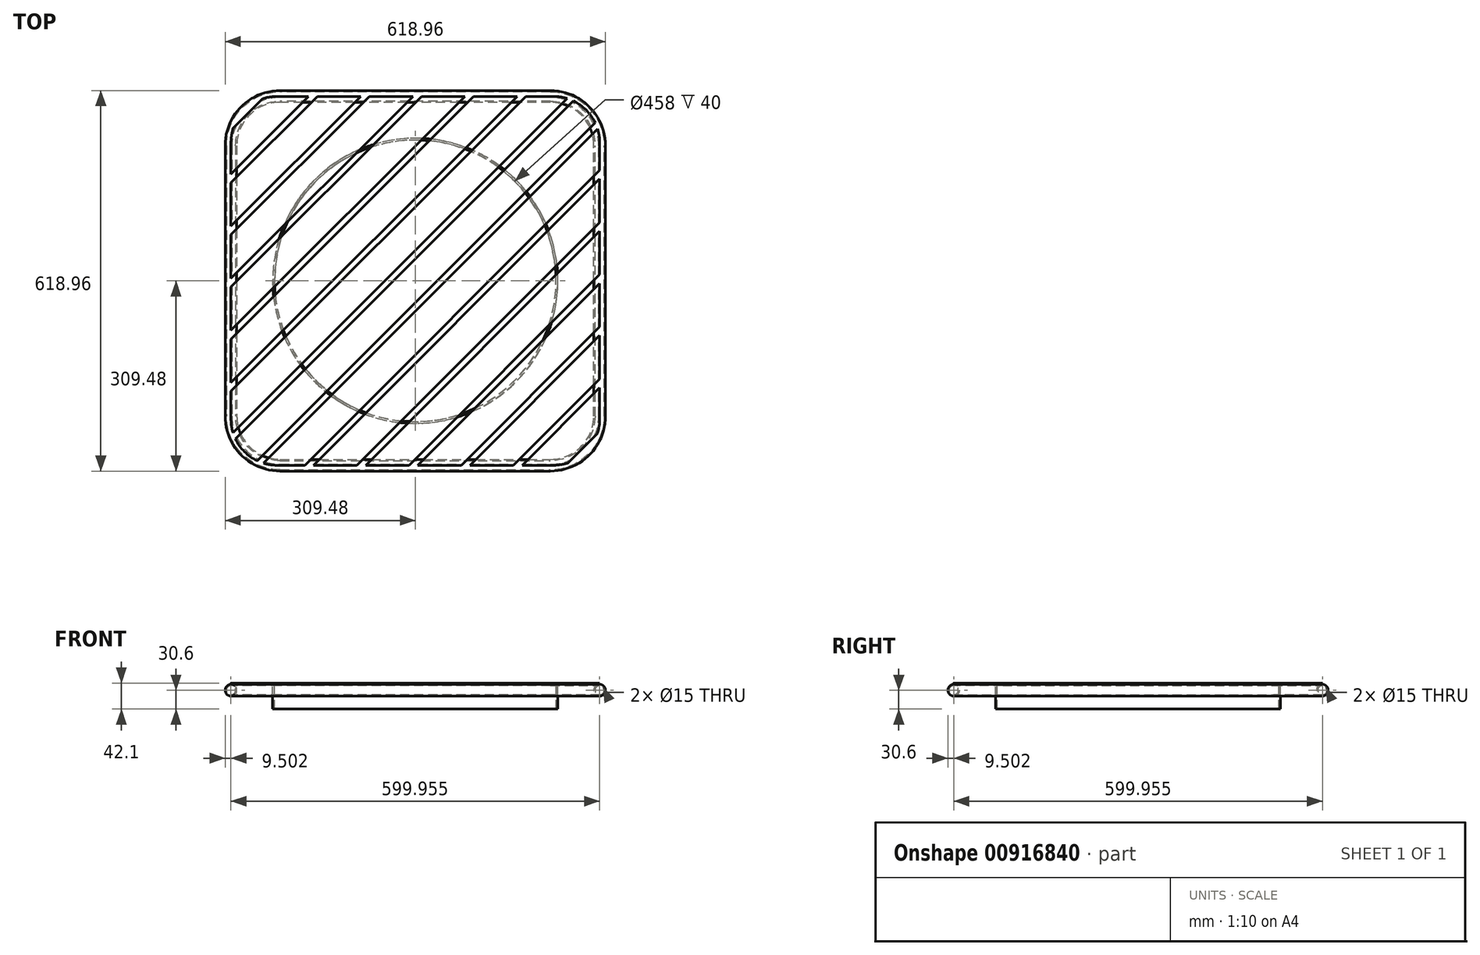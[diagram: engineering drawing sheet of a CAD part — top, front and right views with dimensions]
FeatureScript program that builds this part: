
annotation { "Feature Type Name" : "Feature", "Feature Type Description" : "" }
export const myFeature = defineFeature(function(context is Context, id is Id, definition is map)
    precondition{}
    {
        {
            var Q0;
            Q0=qCreatedBy(makeId("Top.planeOp"),FACE);
            var sketch = newSketch(context, id + "F0", { "sketchPlane" : qUnion([Q0])});
            skLineSegment(sketch, "E0.bottom", {"start": v(-220, 300) * mm, "end": v(220, 300) * mm});
            skLineSegment(sketch, "E0.top", {"start": v(-220, -300) * mm, "end": v(220, -300) * mm});
            skLineSegment(sketch, "E0.left", {"start": v(-300, 220) * mm, "end": v(-300, -220) * mm});
            skLineSegment(sketch, "E0.right", {"start": v(300, 220) * mm, "end": v(300, -220) * mm});
            skPoint(sketch, "E0.middle", {"position": v(0, 0) * mm});
            skArc(sketch, "E1", {"start": v(-220, 300) * mm, "mid": v(-276.57, 276.57) * mm, "end": v(-300, 220) * mm});
            skArc(sketch, "E2", {"start": v(300, 220) * mm, "mid": v(276.57, 276.57) * mm, "end": v(220, 300) * mm});
            skPoint(sketch, "E3.orphan", {"position": v(-300, 300) * mm});
            skPoint(sketch, "E4.orphan", {"position": v(300, 300) * mm});
            skArc(sketch, "E5.MirrorCS", {"start": v(300, -220) * mm, "mid": v(276.57, -276.57) * mm, "end": v(220, -300) * mm});
            skArc(sketch, "E6.MirrorCS", {"start": v(-220, -300) * mm, "mid": v(-276.57, -276.57) * mm, "end": v(-300, -220) * mm});
            skPoint(sketch, "E7.orphan", {"position": v(-300, -300) * mm});
            skPoint(sketch, "E8.orphan", {"position": v(300, -300) * mm});
            skSolve(sketch);
        }
        {
            var Q0;
            Q0=qCreatedBy(makeId("Front.planeOp"),FACE);
            var sketch = newSketch(context, id + "F1", { "sketchPlane" : qUnion([Q0])});
            skCircle(sketch, "E9", {"center": v(-299.98, 0) * mm, "radius": 9.5 * mm});
            skCircle(sketch, "E10", {"center": v(-299.98, 0) * mm, "radius": 7.5 * mm});
            skSolve(sketch);
        }
        {
            var Q0;
            Q0=makeQuery(id+"F1.imprint","IMPRINT",FACE,{"disambiguationData":[TD([[makeQuery(id+"F1.imprint","IMPRINT",EDGE,{"derivedFrom":sQuery(id+"F1.wireOp",EDGE,"E9")}),1.0]])]});
            var Q1;
            Q1=sQuery(id+"F0.wireOp",EDGE,"E0.left");
            var Q2;
            Q2=sQuery(id+"F0.wireOp",EDGE,"E1");
            var Q3;
            Q3=sQuery(id+"F0.wireOp",EDGE,"E0.bottom");
            var Q4;
            Q4=sQuery(id+"F0.wireOp",EDGE,"E2");
            var Q5;
            Q5=sQuery(id+"F0.wireOp",EDGE,"E0.right");
            var Q6;
            Q6=sQuery(id+"F0.wireOp",EDGE,"E5.MirrorCS");
            var Q7;
            Q7=sQuery(id+"F0.wireOp",EDGE,"E0.top");
            var Q8;
            Q8=sQuery(id+"F0.wireOp",EDGE,"E6.MirrorCS");
            sweep(context, id + "F2", {"profiles" : qUnion([Q0]), "path" : qUnion([Q1, Q2, Q3, Q4, Q5, Q6, Q7, Q8])});
        }
        {
            var Q0;
            Q0=qCreatedBy(makeId("Top.planeOp"),FACE);
            cPlane(context, id + "F3", {"entities" : qUnion([Q0]), "cplaneType" : CPlaneType.OFFSET, "offset" : 9.5 * mm, "width" : 150 * mm, "height" : 150 * mm});
        }
        {
            var Q0;
            Q0=qCreatedBy(id+"F3.planeOp",FACE);
            var sketch = newSketch(context, id + "F4", { "sketchPlane" : qUnion([Q0])});
            skLineSegment(sketch, "E11.bottom", {"start": v(-225, 300) * mm, "end": v(225, 300) * mm});
            skLineSegment(sketch, "E11.top", {"start": v(-225, -300) * mm, "end": v(225, -300) * mm});
            skLineSegment(sketch, "E11.left", {"start": v(-300, 225) * mm, "end": v(-300, -225) * mm});
            skLineSegment(sketch, "E11.right", {"start": v(300, 225) * mm, "end": v(300, -225) * mm});
            skPoint(sketch, "E11.middle", {"position": v(0, 0) * mm});
            skArc(sketch, "E12", {"start": v(-225, 300) * mm, "mid": v(-278.03, 278.03) * mm, "end": v(-300, 225) * mm});
            skArc(sketch, "E13", {"start": v(300, 225) * mm, "mid": v(278.03, 278.03) * mm, "end": v(225, 300) * mm});
            skPoint(sketch, "E14.orphan", {"position": v(-300, 300) * mm});
            skPoint(sketch, "E15.orphan", {"position": v(300, 300) * mm});
            skArc(sketch, "E16.MirrorCS", {"start": v(-225, -300) * mm, "mid": v(-278.03, -278.03) * mm, "end": v(-300, -225) * mm});
            skArc(sketch, "E17.MirrorCS", {"start": v(300, -225) * mm, "mid": v(278.03, -278.03) * mm, "end": v(225, -300) * mm});
            skPoint(sketch, "E18.orphan", {"position": v(-300, -300) * mm});
            skPoint(sketch, "E19.orphan", {"position": v(300, -300) * mm});
            skLineSegment(sketch, "E20", {"start": v(-300, 74.77) * mm, "end": v(-74.77, 300) * mm});
            skLineSegment(sketch, "E21", {"start": v(-4.06, 300) * mm, "end": v(-300, 4.06) * mm});
            skLineSegment(sketch, "E22", {"start": v(10.09, 300) * mm, "end": v(-300, -10.09) * mm});
            skLineSegment(sketch, "E23", {"start": v(80.8, 300) * mm, "end": v(-300, -80.8) * mm});
            skLineSegment(sketch, "E24", {"start": v(94.94, 300) * mm, "end": v(-300, -94.94) * mm});
            skLineSegment(sketch, "E25", {"start": v(165.65, 300) * mm, "end": v(-300, -165.65) * mm});
            skLineSegment(sketch, "E26", {"start": v(179.8, 300) * mm, "end": v(-300, -179.8) * mm});
            skLineSegment(sketch, "E27", {"start": v(250.5, 300) * mm, "end": v(-300, -250.5) * mm});
            skLineSegment(sketch, "E28", {"start": v(-292.68, -257.32) * mm, "end": v(257.32, 292.68) * mm});
            skLineSegment(sketch, "E29.MirrorCS", {"start": v(-257.32, -292.68) * mm, "end": v(292.68, 257.32) * mm});
            skLineSegment(sketch, "E30.MirrorCS", {"start": v(296.65, 247.16) * mm, "end": v(-247.16, -296.65) * mm});
            skLineSegment(sketch, "E31.MirrorCS", {"start": v(300, 179.8) * mm, "end": v(-179.8, -300) * mm});
            skLineSegment(sketch, "E32.MirrorCS", {"start": v(300, 165.65) * mm, "end": v(-165.65, -300) * mm});
            skLineSegment(sketch, "E33.MirrorCS", {"start": v(300, 94.94) * mm, "end": v(-94.94, -300) * mm});
            skLineSegment(sketch, "E34.MirrorCS", {"start": v(300, 80.8) * mm, "end": v(-80.8, -300) * mm});
            skLineSegment(sketch, "E35.MirrorCS", {"start": v(300, 10.09) * mm, "end": v(-10.09, -300) * mm});
            skLineSegment(sketch, "E36.MirrorCS", {"start": v(300, -4.06) * mm, "end": v(4.06, -300) * mm});
            skLineSegment(sketch, "E37.MirrorCS", {"start": v(74.77, -300) * mm, "end": v(300, -74.77) * mm});
            skLineSegment(sketch, "E38", {"start": v(300, -88.9) * mm, "end": v(88.9, -300) * mm});
            skLineSegment(sketch, "E39", {"start": v(300, -159.62) * mm, "end": v(159.62, -300) * mm});
            skLineSegment(sketch, "E40", {"start": v(300, -173.76) * mm, "end": v(173.76, -300) * mm});
            skLineSegment(sketch, "E41", {"start": v(-225, -225) * mm, "end": v(225, 225) * mm});
            skLineSegment(sketch, "E42", {"start": v(300, -244.47) * mm, "end": v(244.47, -300) * mm});
            skLineSegment(sketch, "E43.MirrorCS", {"start": v(-244.47, 300) * mm, "end": v(-300, 244.47) * mm});
            skLineSegment(sketch, "E44.MirrorCS", {"start": v(-173.76, 300) * mm, "end": v(-300, 173.76) * mm});
            skLineSegment(sketch, "E45.MirrorCS", {"start": v(-159.62, 300) * mm, "end": v(-300, 159.62) * mm});
            skLineSegment(sketch, "E46.MirrorCS", {"start": v(-88.9, 300) * mm, "end": v(-300, 88.9) * mm});
            skSolve(sketch);
        }
        {
            var Q0;
            {var subQ0=sQuery(id+"F4.wireOp",EDGE,"E20");Q0=makeQuery(id+"F4.imprint","IMPRINT",FACE,{"disambiguationData":[TD([[makeQuery(id+"F4.imprint","IMPRINT",EDGE,{"derivedFrom":subQ0}),-1.0]])]});}
            var Q1;
            {var subQ0=sQuery(id+"F4.wireOp",EDGE,"E22");Q1=makeQuery(id+"F4.imprint","IMPRINT",FACE,{"disambiguationData":[TD([[makeQuery(id+"F4.imprint","IMPRINT",EDGE,{"derivedFrom":subQ0}),1.0]])]});}
            var Q2;
            {var subQ0=sQuery(id+"F4.wireOp",EDGE,"E24");Q2=makeQuery(id+"F4.imprint","IMPRINT",FACE,{"disambiguationData":[TD([[makeQuery(id+"F4.imprint","IMPRINT",EDGE,{"derivedFrom":subQ0}),1.0]])]});}
            var Q3;
            {var subQ0=sQuery(id+"F4.wireOp",EDGE,"E26");Q3=makeQuery(id+"F4.imprint","IMPRINT",FACE,{"disambiguationData":[TD([[makeQuery(id+"F4.imprint","IMPRINT",EDGE,{"derivedFrom":subQ0}),1.0]])]});}
            var Q4;
            {var subQ0=sQuery(id+"F4.wireOp",EDGE,"f3e3acb9-5dc7-480f-a169-b6047dde436d0.MirrorCS");Q4=makeQuery(id+"F4.imprint","IMPRINT",FACE,{"disambiguationData":[TD([[makeQuery(id+"F4.imprint","IMPRINT",EDGE,{"derivedFrom":subQ0}),1.0]])]});}
            var Q5;
            {var subQ0=sQuery(id+"F4.wireOp",EDGE,"8c5f72dc-6430-4fd1-9669-a3bc66972e370.MirrorCS");Q5=makeQuery(id+"F4.imprint","IMPRINT",FACE,{"disambiguationData":[TD([[makeQuery(id+"F4.imprint","IMPRINT",EDGE,{"derivedFrom":subQ0}),1.0]])]});}
            var Q6;
            {var subQ0=sQuery(id+"F4.wireOp",EDGE,"5638e17f-524b-40a8-8cfa-9c4565ae56270.MirrorCS");Q6=makeQuery(id+"F4.imprint","IMPRINT",FACE,{"disambiguationData":[TD([[makeQuery(id+"F4.imprint","IMPRINT",EDGE,{"derivedFrom":subQ0}),1.0]])]});}
            var Q7;
            {var subQ0=sQuery(id+"F4.wireOp",EDGE,"d3d81764-08a6-4486-8bd4-b46154aa33660.MirrorCS");Q7=makeQuery(id+"F4.imprint","IMPRINT",FACE,{"disambiguationData":[TD([[makeQuery(id+"F4.imprint","IMPRINT",EDGE,{"derivedFrom":subQ0}),1.0]])]});}
            var Q8;
            {var subQ0=sQuery(id+"F4.wireOp",EDGE,"Kz8hN87C-jPTE-dKEJ-GhUn-43Xg0fKDj0rT");Q8=makeQuery(id+"F4.imprint","IMPRINT",FACE,{"disambiguationData":[TD([[makeQuery(id+"F4.imprint","IMPRINT",EDGE,{"derivedFrom":subQ0}),-1.0]])]});}
            var Q9;
            {var subQ0=sQuery(id+"F4.wireOp",EDGE,"E30.MirrorCS");Q9=makeQuery(id+"F4.imprint","IMPRINT",FACE,{"disambiguationData":[TD([[makeQuery(id+"F4.imprint","IMPRINT",EDGE,{"derivedFrom":subQ0}),1.0]])]});}
            var Q10;
            {var subQ0=sQuery(id+"F4.wireOp",EDGE,"E32.MirrorCS");Q10=makeQuery(id+"F4.imprint","IMPRINT",FACE,{"disambiguationData":[TD([[makeQuery(id+"F4.imprint","IMPRINT",EDGE,{"derivedFrom":subQ0}),1.0]])]});}
            var Q11;
            {var subQ0=sQuery(id+"F4.wireOp",EDGE,"E34.MirrorCS");Q11=makeQuery(id+"F4.imprint","IMPRINT",FACE,{"disambiguationData":[TD([[makeQuery(id+"F4.imprint","IMPRINT",EDGE,{"derivedFrom":subQ0}),1.0]])]});}
            var Q12;
            {var subQ0=sQuery(id+"F4.wireOp",EDGE,"E36.MirrorCS");Q12=makeQuery(id+"F4.imprint","IMPRINT",FACE,{"disambiguationData":[TD([[makeQuery(id+"F4.imprint","IMPRINT",EDGE,{"derivedFrom":subQ0}),1.0]])]});}
            var Q13;
            {var subQ0=sQuery(id+"F4.wireOp",EDGE,"E38");Q13=makeQuery(id+"F4.imprint","IMPRINT",FACE,{"disambiguationData":[TD([[makeQuery(id+"F4.imprint","IMPRINT",EDGE,{"derivedFrom":subQ0}),1.0]])]});}
            var Q14;
            {var subQ6=sQuery(id+"F4.wireOp",EDGE,"E40");Q14=makeQuery(id+"F4.imprint","IMPRINT",FACE,{"disambiguationData":[TD([[makeQuery(id+"F4.imprint","IMPRINT",EDGE,{"derivedFrom":subQ6}),1.0]])]});}
            var Q15;
            {var subQ0=sQuery(id+"F4.wireOp",EDGE,"E45.MirrorCS");Q15=makeQuery(id+"F4.imprint","IMPRINT",FACE,{"disambiguationData":[TD([[makeQuery(id+"F4.imprint","IMPRINT",EDGE,{"derivedFrom":subQ0}),1.0]])]});}
            var Q16;
            {var subQ3=sQuery(id+"F4.wireOp",EDGE,"E43.MirrorCS");Q16=makeQuery(id+"F4.imprint","IMPRINT",FACE,{"disambiguationData":[TD([[makeQuery(id+"F4.imprint","IMPRINT",EDGE,{"derivedFrom":subQ3}),1.0]])]});}
            var Q17;
            {var subQ0=sQuery(id+"F4.wireOp",EDGE,"E28");Q17=makeQuery(id+"F4.imprint","IMPRINT",FACE,{"disambiguationData":[TD([[makeQuery(id+"F4.imprint","IMPRINT",EDGE,{"derivedFrom":subQ0}),-1.0]])]});}
            var Q18;
            {var subQ7=sQuery(id+"F4.wireOp",EDGE,"2fb49efd-54a2-4a6d-895c-4ce7ffd1ea3b0.MirrorCS");Q18=makeQuery(id+"F4.imprint","IMPRINT",FACE,{"disambiguationData":[TD([[makeQuery(id+"F4.imprint","IMPRINT",EDGE,{"derivedFrom":subQ7}),1.0]])]});}
            var Q19;
            {var subQ8=sQuery(id+"F4.wireOp",EDGE,"YEpJIx5I-sweu-1O3q-sWPA-YcQCGaNAEn4W");Q19=makeQuery(id+"F4.imprint","IMPRINT",FACE,{"disambiguationData":[TD([[makeQuery(id+"F4.imprint","IMPRINT",EDGE,{"derivedFrom":subQ8}),-1.0]])]});}
            extrude(context, id + "F5", {"entities" : qUnion([Q0, Q1, Q2, Q3, Q4, Q5, Q6, Q7, Q8, Q9, Q10, Q11, Q12, Q13, Q14, Q15, Q16, Q17, Q18, Q19]), "operationType" : NewBodyOperationType.ADD, "depth" : 2 * mm, "offsetDistance" : 25 * mm, "hasSecondDirection" : true, "secondDirectionOppositeDirection" : true, "secondDirectionDepth" : .1 * mm});
        }
        {
            var Q0;
            Q0=makeQuery(id+"F5.opExtrude","CAP_FACE",FACE,{"disambiguationData":[OSD([sQuery(id+"F4.wireOp",EDGE,"E11.top"),sQuery(id+"F4.wireOp",EDGE,"E11.right"),sQuery(id+"F4.wireOp",EDGE,"E34.MirrorCS"),sQuery(id+"F4.wireOp",EDGE,"E35.MirrorCS")])],"isStart":true});
            var sketch = newSketch(context, id + "F6", { "sketchPlane" : qUnion([Q0])});
            skCircle(sketch, "E47", {"center": v(0, 0) * mm, "radius": 229 * mm});
            skCircle(sketch, "E48", {"center": v(0, 0) * mm, "radius": 232 * mm});
            skSolve(sketch);
        }
        {
            var Q0;
            Q0=qSketchRegion(id+"F6",true);
            extrude(context, id + "F7", {"entities" : qUnion([Q0]), "operationType" : NewBodyOperationType.ADD, "depth" : 40 * mm, "offsetDistance" : 25 * mm});
        }
    });
